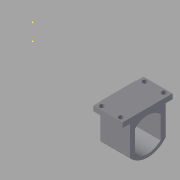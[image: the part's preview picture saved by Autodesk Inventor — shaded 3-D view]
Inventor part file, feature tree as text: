
AUTODESK INVENTOR PART (.ipt)
format: ipt  version: 2015 (Build 190159000, 159)  size: 242,688 bytes
history: native  units: in
note: dims shown in document units (in); Inventor stores cm internally (conversion verified against a paired STEP export)
features: sketch x15, extrude x13, fillet x2, plane x1, pattern_circular x1
ambient origin geometry x8: Origin, YZ Plane, XZ Plane, XY Plane, X Axis, Y Axis, Z Axis, Center Point
bodies: Solid1 (feature_tree)
feature tree (32):
  extrude  "Extrusion1"  Depth=0.1181in
  fillet  "Fillet1"  Radius=0.1969in
  fillet  "Fillet2"  [1 undecoded]
  plane  "Work Plane1"
  extrude  "Extrusion3"  Depth=0.1181in
  pattern_circular  "Circular Pattern1"  Count=4 Angle=360.0deg
  extrude  "Extrusion5"  Depth=0.1181in TaperAngle=0.0deg
  extrude  "Extrusion6"  Depth=0.1181in TaperAngle=0.0deg
  extrude  "Extrusion7"  Depth=0.3937in TaperAngle=0.0deg
  sketch  "Sketch11"  dims[d39=0.1969in d40=0.1181in d41=0.0in]
  extrude  "Extrusion8"  Depth=3.937in TaperAngle=0.0deg
  extrude  "Extrusion9"  Depth=0.1181in TaperAngle=0.0deg
  extrude  "Extrusion10"  Depth=0.5512in
  sketch  "Sketch15"  dims[d53=0.5118in d54=0.0in d55=0.5512in]
  extrude  "Extrusion11"  Depth=0.7087in
  extrude  "Extrusion12"  Depth=0.3937in
  extrude  "Extrusion13"  Depth=0.1181in TaperAngle=0.0deg
  extrude  "Extrusion14"  Depth=0.1181in
  extrude  "Extrusion15"  Depth=0.1181in TaperAngle=0.0deg
  sketch  "Sketch1"  dims[d4=0.1181in d5=0.0in d6=0.1969in d7=0.1969in d8=-0.1969in]
  sketch  "Sketch6"  dims[d17=0.7087in d21=0.1181in]
  sketch  "Sketch8"  dims[d22=0.1181in]
  sketch  "Sketch9"  dims[d24=0.7087in d25=0.0in d26=1.5748in d27=360.0deg]
  sketch  "Sketch10"  dims[d35=0.1969in d36=0.1181in d37=0.0in]
  sketch  "Sketch12"  dims[d42=0.3937in d43=0.0in d44=3.937in d45=0.0in]
  sketch  "Sketch13"  dims[d46=3.937in d47=0.0in d48=3.937in d49=0.0in]
  sketch  "Sketch14"  dims[d50=0.1181in d51=3.937in d52=0.0in]
  sketch  "Sketch17"  dims[d56=0.126in d57=0.7087in]
  sketch  "Sketch18"  dims[d58=0.3937in d59=0.3937in]
  sketch  "Sketch20"  dims[d60=0.7087in d61=0.0in d62=0.1181in d63=0.0in]
  sketch  "Sketch22"  dims[d64=0.1181in d65=0.1181in]
  sketch  "Sketch23"  dims[d66=0.1181in d67=0.1575in d68=0.0in]
note: 1 required parameter value undecoded (feature->parameter linkage not recoverable at this tier; creation-order binding heuristic only, values carry confidence <= 0.55)
